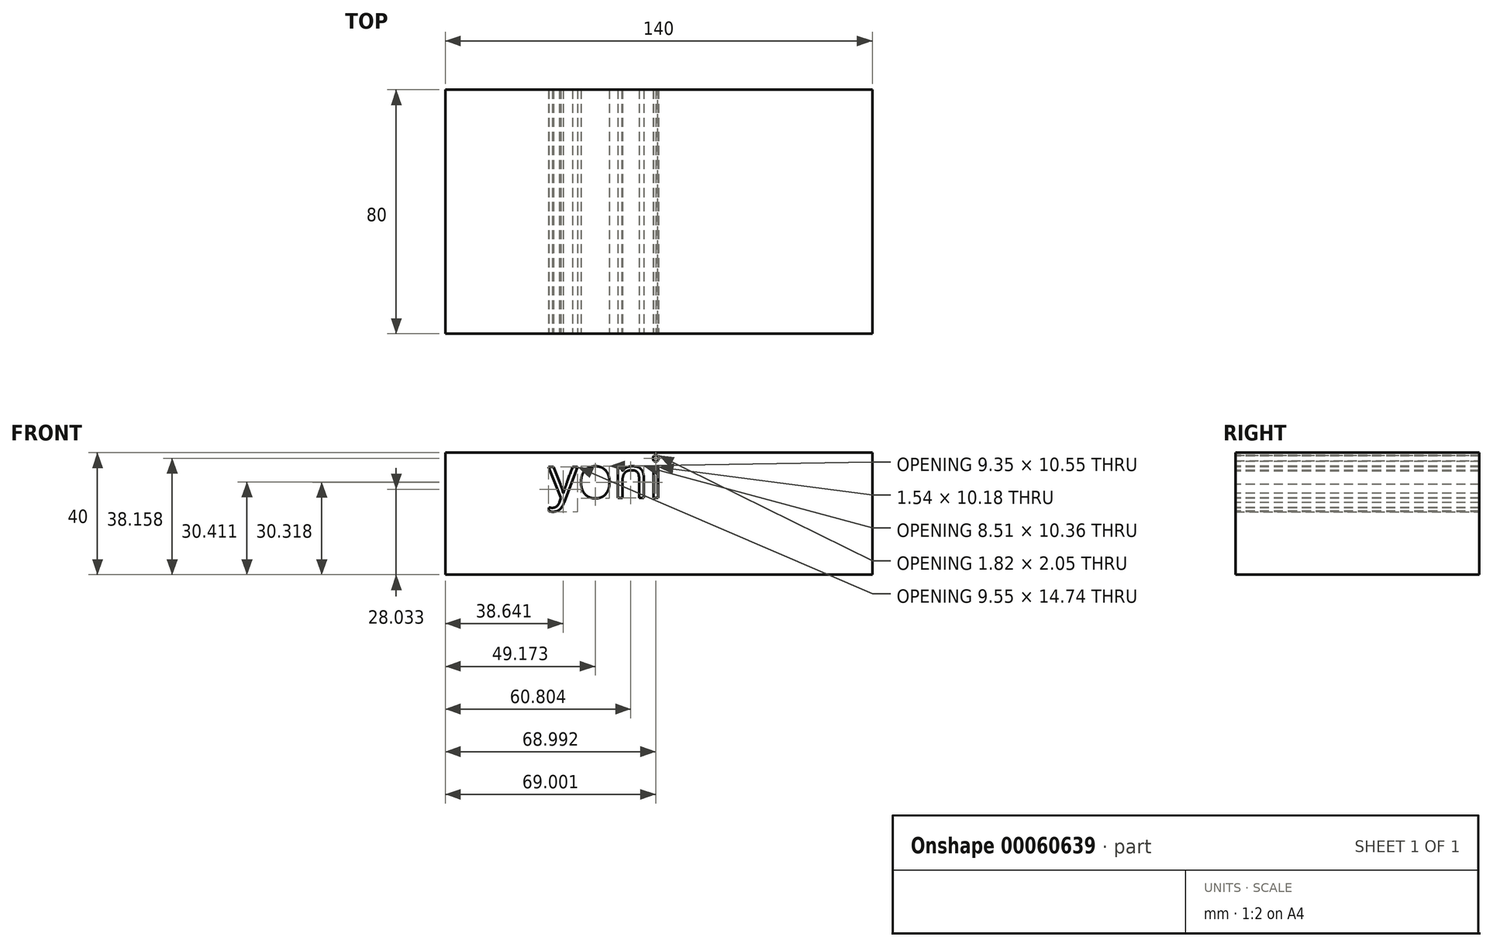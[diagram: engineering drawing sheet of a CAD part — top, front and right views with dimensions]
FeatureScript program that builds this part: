
annotation { "Feature Type Name" : "Feature", "Feature Type Description" : "" }
export const myFeature = defineFeature(function(context is Context, id is Id, definition is map)
    precondition{}
    {
        {
            var Q0;
            Q0=qCreatedBy(makeId("Top.planeOp"),FACE);
            var sketch = newSketch(context, id + "F0", { "sketchPlane" : qUnion([Q0])});
            skLineSegment(sketch, "E0.rect.bottom", {"start": v(-70, -40) * mm, "end": v(70, -40) * mm});
            skLineSegment(sketch, "E0.rect.top", {"start": v(-70, 40) * mm, "end": v(70, 40) * mm});
            skLineSegment(sketch, "E0.rect.left", {"start": v(-70, -40) * mm, "end": v(-70, 40) * mm});
            skLineSegment(sketch, "E0.rect.right", {"start": v(70, -40) * mm, "end": v(70, 40) * mm});
            skPoint(sketch, "E0.rect.middle", {"position": v(0, 0) * mm});
            skSolve(sketch);
        }
        {
            var Q0;
            Q0=makeQuery(id+"F0.imprint","IMPRINT",FACE,{"disambiguationData":[TD([[makeQuery(id+"F0.imprint","IMPRINT",EDGE,{"derivedFrom":sQuery(id+"F0.wireOp",EDGE,"E0.rect.bottom")}),1.0]])]});
            extrude(context, id + "F1", {"entities" : qUnion([Q0]), "depth" : 40 * mm});
        }
        {
            var Q0;
            Q0=makeQuery(id+"F1.opExtrude","SWEPT_FACE",FACE,{"disambiguationData":[OSD([sQuery(id+"F0.wireOp",EDGE,"E0.rect.bottom")])]});
            var sketch = newSketch(context, id + "F2", { "sketchPlane" : qUnion([Q0])});
            skText(sketch, "E1", { "text": "yoni\n", "fontName": "OpenSans-Regular.ttf"});
            const initialGuessF2  = {"E1": [-0.03615, 0.02523, 1, 0, 0.01369]};
            skSetInitialGuess(sketch, initialGuessF2);
            skSolve(sketch);
        }
        {
            var Q0;
            Q0 = qSketchRegion(id + "F2", true);
            extrude(context, id + "F3", {"entities" : qUnion([Q0]), "operationType" : NewBodyOperationType.REMOVE, "endBound" : BoundingType.SYMMETRIC, "oppositeDirection" : true, "depth" : 10000 * mm});
        }
        {
            var Q0;
            Q0=makeQuery(id+"F3.boolean.opBoolean","SPLIT",FACE,{"disambiguationData":[TD([makeQuery(id+"F3.opExtrude","SWEPT_FACE",FACE,{"disambiguationData":[OSD([sQuery(id+"F2.wireOp",EDGE,"E1.sketch_text.stroke-25")])]})])],"derivedFrom":makeQuery(id+"F1.opExtrude","SWEPT_FACE",FACE,{"disambiguationData":[OSD([sQuery(id+"F0.wireOp",EDGE,"E0.rect.bottom")])]})});
            extrude(context, id + "F4", {"entities" : qUnion([Q0]), "operationType" : NewBodyOperationType.REMOVE, "endBound" : BoundingType.THROUGH_ALL, "oppositeDirection" : true, "depth" : 25 * mm});
        }
    });
